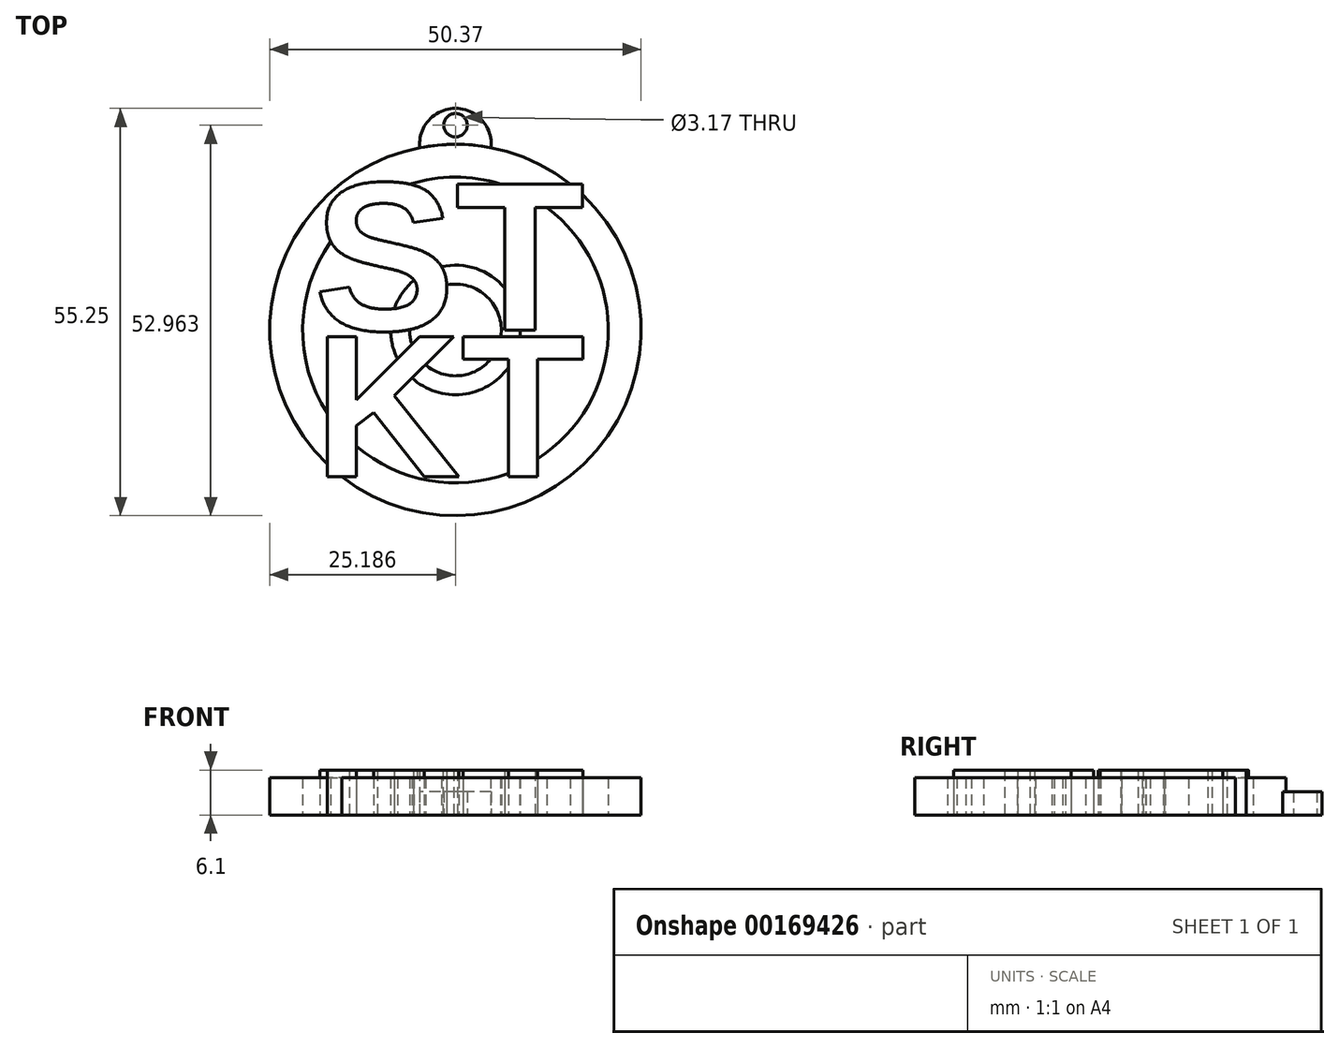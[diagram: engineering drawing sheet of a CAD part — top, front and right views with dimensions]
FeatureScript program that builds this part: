
annotation { "Feature Type Name" : "Feature", "Feature Type Description" : "" }
export const myFeature = defineFeature(function(context is Context, id is Id, definition is map)
    precondition{}
    {
        {
            var Q0;
            Q0=qCreatedBy(makeId("Top.planeOp"),FACE);
            var sketch = newSketch(context, id + "F0", { "sketchPlane" : qUnion([Q0])});
            skText(sketch, "E0", { "text": "ST", "fontName": "Arimo-Bold.ttf"});
            skText(sketch, "E1", { "text": "KT", "fontName": "Arimo-Bold.ttf"});
            skCircle(sketch, "E2", {"center": v(10.39, -1.09) * mm, "radius": 20.73 * mm});
            skCircle(sketch, "E3", {"center": v(10.39, -1.09) * mm, "radius": 25.19 * mm});
            skCircle(sketch, "E4", {"center": v(10.39, 26.68) * mm, "radius": 1.59 * mm});
            skArc(sketch, "E5", {"start": v(15.23, 23.63) * mm, "mid": v(10.39, 28.97) * mm, "end": v(5.54, 23.63) * mm});
            skCircle(sketch, "E6", {"center": v(10.39, -1.09) * mm, "radius": 6.22 * mm});
            skCircle(sketch, "E7", {"center": v(10.39, -1.09) * mm, "radius": 8.79 * mm});
            const initialGuessF0  = {"E0": [-0.00886, -0.00109, 1, 0, 0.02073], "E1": [-0.00886, -0.021, 1, 0, 0.0199]};
            skSetInitialGuess(sketch, initialGuessF0);
            skSolve(sketch);
        }
        {
            var Q0;
            {var subQ0=sQuery(id+"F0.wireOp",EDGE,"E0.sketch_text.stroke-31");Q0=makeQuery(id+"F0.imprint","IMPRINT",FACE,{"disambiguationData":[TD([[makeQuery(id+"F0.imprint","IMPRINT",EDGE,{"derivedFrom":subQ0}),-1.0]])]});}
            var Q1;
            {var subQ1=sQuery(id+"F0.wireOp",EDGE,"E0.sketch_text.stroke-36");var subQ7=sQuery(id+"F0.wireOp",EDGE,"E3");var subQ9=makeQuery(id+"F0.imprint","INTERSECT",VERTEX,{"derivedFrom":[subQ1,subQ7]});Q1=makeQuery(id+"F0.imprint","IMPRINT",FACE,{"disambiguationData":[TD([[makeQuery(id+"F0.imprint","IMPRINT",EDGE,{"disambiguationData":[TD([[subQ9,1.0]])],"derivedFrom":subQ1}),-1.0]])]});}
            var Q2;
            {var subQ0=sQuery(id+"F0.wireOp",EDGE,"E0.sketch_text.stroke-37");var subQ1=sQuery(id+"F0.wireOp",EDGE,"E0.sketch_text.stroke-36");var subQ2=makeQuery(id+"F0.imprint","INTERSECT",VERTEX,{"derivedFrom":[subQ1,subQ0]});Q2=makeQuery(id+"F0.imprint","IMPRINT",FACE,{"disambiguationData":[TD([[makeQuery(id+"F0.imprint","IMPRINT",EDGE,{"disambiguationData":[TD([[subQ2,1.0]])],"derivedFrom":subQ1}),-1.0]])]});}
            var Q3;
            {var subQ6=sQuery(id+"F0.wireOp",EDGE,"E0.sketch_text.stroke-15");Q3=makeQuery(id+"F0.imprint","IMPRINT",FACE,{"disambiguationData":[TD([[makeQuery(id+"F0.imprint","IMPRINT",EDGE,{"derivedFrom":subQ6}),-1.0]])]});}
            var Q4;
            {var subQ0=sQuery(id+"F0.wireOp",EDGE,"E0.sketch_text.stroke-19");Q4=makeQuery(id+"F0.imprint","IMPRINT",FACE,{"disambiguationData":[TD([[makeQuery(id+"F0.imprint","IMPRINT",EDGE,{"derivedFrom":subQ0}),-1.0]])]});}
            var Q5;
            Q5=makeQuery(id+"F0.imprint","IMPRINT",FACE,{"disambiguationData":[TD([[makeQuery(id+"F0.imprint","IMPRINT",EDGE,{"derivedFrom":sQuery(id+"F0.wireOp",EDGE,"E0.sketch_text.stroke-0")}),-1.0]])]});
            var Q6;
            Q6=makeQuery(id+"F0.imprint","IMPRINT",FACE,{"disambiguationData":[TD([[makeQuery(id+"F0.imprint","IMPRINT",EDGE,{"derivedFrom":sQuery(id+"F0.wireOp",EDGE,"E1.sketch_text.stroke-0")}),-1.0]])]});
            var Q7;
            {var subQ0=sQuery(id+"F0.wireOp",EDGE,"E1.sketch_text.stroke-15");Q7=makeQuery(id+"F0.imprint","IMPRINT",FACE,{"disambiguationData":[TD([[makeQuery(id+"F0.imprint","IMPRINT",EDGE,{"derivedFrom":subQ0}),-1.0]])]});}
            var Q8;
            {var subQ1=sQuery(id+"F0.wireOp",EDGE,"E1.sketch_text.stroke-2");var subQ7=sQuery(id+"F0.wireOp",EDGE,"E1.sketch_text.stroke-3");var subQ8=makeQuery(id+"F0.imprint","INTERSECT",VERTEX,{"derivedFrom":[subQ1,subQ7]});Q8=makeQuery(id+"F0.imprint","IMPRINT",FACE,{"disambiguationData":[TD([[makeQuery(id+"F0.imprint","IMPRINT",EDGE,{"disambiguationData":[TD([[subQ8,1.0]])],"derivedFrom":subQ1}),-1.0]])]});}
            var Q9;
            {var subQ0=sQuery(id+"F0.wireOp",EDGE,"E1.sketch_text.stroke-4");var subQ1=sQuery(id+"F0.wireOp",EDGE,"E1.sketch_text.stroke-3");var subQ2=makeQuery(id+"F0.imprint","INTERSECT",VERTEX,{"derivedFrom":[subQ1,subQ0]});Q9=makeQuery(id+"F0.imprint","IMPRINT",FACE,{"disambiguationData":[TD([[makeQuery(id+"F0.imprint","IMPRINT",EDGE,{"disambiguationData":[TD([[subQ2,1.0]])],"derivedFrom":subQ1}),-1.0]])]});}
            var Q10;
            {var subQ0=sQuery(id+"F0.wireOp",EDGE,"E1.sketch_text.stroke-13");Q10=makeQuery(id+"F0.imprint","IMPRINT",FACE,{"disambiguationData":[TD([[makeQuery(id+"F0.imprint","IMPRINT",EDGE,{"derivedFrom":subQ0}),-1.0]])]});}
            var Q11;
            {var subQ4=sQuery(id+"F0.wireOp",EDGE,"E0.sketch_text.stroke-9");Q11=makeQuery(id+"F0.imprint","IMPRINT",FACE,{"disambiguationData":[TD([[makeQuery(id+"F0.imprint","IMPRINT",EDGE,{"derivedFrom":subQ4}),-1.0]])]});}
            var Q12;
            {var subQ0=sQuery(id+"F0.wireOp",EDGE,"E0.sketch_text.stroke-2");Q12=makeQuery(id+"F0.imprint","IMPRINT",FACE,{"disambiguationData":[TD([[makeQuery(id+"F0.imprint","IMPRINT",EDGE,{"derivedFrom":subQ0}),-1.0]])]});}
            var Q13;
            {var subQ5=sQuery(id+"F0.wireOp",EDGE,"E0.sketch_text.stroke-1");var subQ12=sQuery(id+"F0.wireOp",EDGE,"E6");var subQ13=makeQuery(id+"F0.imprint","INTERSECT",VERTEX,{"derivedFrom":[subQ5,subQ12]});Q13=makeQuery(id+"F0.imprint","IMPRINT",FACE,{"disambiguationData":[TD([[makeQuery(id+"F0.imprint","IMPRINT",EDGE,{"disambiguationData":[TD([[subQ13,-1.0]])],"derivedFrom":subQ5}),-1.0]])]});}
            var Q14;
            {var subQ0=sQuery(id+"F0.wireOp",EDGE,"E7");var subQ1=sQuery(id+"F0.wireOp",EDGE,"E1.sketch_text.stroke-7");var subQ2=makeQuery(id+"F0.imprint","INTERSECT",VERTEX,{"derivedFrom":[subQ1,subQ0]});Q14=makeQuery(id+"F0.imprint","IMPRINT",FACE,{"disambiguationData":[TD([[makeQuery(id+"F0.imprint","IMPRINT",EDGE,{"disambiguationData":[TD([[subQ2,-1.0]])],"derivedFrom":subQ1}),-1.0]])]});}
            var Q15;
            {var subQ0=sQuery(id+"F0.wireOp",EDGE,"E1.sketch_text.stroke-8");Q15=makeQuery(id+"F0.imprint","IMPRINT",FACE,{"disambiguationData":[TD([[makeQuery(id+"F0.imprint","IMPRINT",EDGE,{"derivedFrom":subQ0}),-1.0]])]});}
            var Q16;
            {var subQ1=sQuery(id+"F0.wireOp",EDGE,"E1.sketch_text.stroke-15");var subQ7=sQuery(id+"F0.wireOp",EDGE,"E1.sketch_text.stroke-14");var subQ8=makeQuery(id+"F0.imprint","INTERSECT",VERTEX,{"derivedFrom":[subQ7,subQ1]});Q16=makeQuery(id+"F0.imprint","IMPRINT",FACE,{"disambiguationData":[TD([[makeQuery(id+"F0.imprint","IMPRINT",EDGE,{"disambiguationData":[TD([[subQ8,1.0]])],"derivedFrom":subQ7}),-1.0]])]});}
            var Q17;
            {var subQ0=sQuery(id+"F0.wireOp",EDGE,"E1.sketch_text.stroke-18");Q17=makeQuery(id+"F0.imprint","IMPRINT",FACE,{"disambiguationData":[TD([[makeQuery(id+"F0.imprint","IMPRINT",EDGE,{"derivedFrom":subQ0}),-1.0]])]});}
            var Q18;
            {var subQ0=sQuery(id+"F0.wireOp",EDGE,"E0.sketch_text.stroke-33");var subQ1=sQuery(id+"F0.wireOp",EDGE,"E0.sketch_text.stroke-32");var subQ2=makeQuery(id+"F0.imprint","INTERSECT",VERTEX,{"derivedFrom":[subQ1,subQ0]});Q18=makeQuery(id+"F0.imprint","IMPRINT",FACE,{"disambiguationData":[TD([[makeQuery(id+"F0.imprint","IMPRINT",EDGE,{"disambiguationData":[TD([[subQ2,1.0]])],"derivedFrom":subQ1}),-1.0]])]});}
            extrude(context, id + "F1", {"entities" : qUnion([Q0, Q1, Q2, Q3, Q4, Q5, Q6, Q7, Q8, Q9, Q10, Q11, Q12, Q13, Q14, Q15, Q16, Q17, Q18]), "depth" : 6.1 * mm});
        }
        {
            var Q0;
            {var subQ15=sQuery(id+"F0.wireOp",EDGE,"E0.sketch_text.stroke-15");Q0=makeQuery(id+"F0.imprint","IMPRINT",FACE,{"disambiguationData":[TD([[makeQuery(id+"F0.imprint","IMPRINT",EDGE,{"derivedFrom":subQ15}),1.0]])]});}
            var Q1;
            {var subQ14=sQuery(id+"F0.wireOp",EDGE,"E1.sketch_text.stroke-13");Q1=makeQuery(id+"F0.imprint","IMPRINT",FACE,{"disambiguationData":[TD([[makeQuery(id+"F0.imprint","IMPRINT",EDGE,{"derivedFrom":subQ14}),1.0]])]});}
            extrude(context, id + "F2", {"entities" : qUnion([Q0, Q1]), "operationType" : NewBodyOperationType.ADD, "depth" : 5.08 * mm});
        }
        {
            var Q0;
            Q0=makeQuery(id+"F0.imprint","IMPRINT",FACE,{"disambiguationData":[TD([[makeQuery(id+"F0.imprint","IMPRINT",EDGE,{"derivedFrom":sQuery(id+"F0.wireOp",EDGE,"E4")}),-1.0]])]});
            extrude(context, id + "F3", {"entities" : qUnion([Q0]), "operationType" : NewBodyOperationType.ADD, "depth" : 3.17 * mm});
        }
        {
            var Q0;
            {var subQ5=sQuery(id+"F0.wireOp",EDGE,"E0.sketch_text.stroke-30");var subQ6=sQuery(id+"F0.wireOp",EDGE,"E0.sketch_text.stroke-29");var subQ7=makeQuery(id+"F0.imprint","INTERSECT",VERTEX,{"derivedFrom":[subQ6,subQ5]});Q0=makeQuery(id+"F0.imprint","IMPRINT",FACE,{"disambiguationData":[TD([[makeQuery(id+"F0.imprint","IMPRINT",EDGE,{"disambiguationData":[TD([[subQ7,1.0]])],"derivedFrom":subQ6}),1.0]])]});}
            var Q1;
            {var subQ0=sQuery(id+"F0.wireOp",EDGE,"E6");var subQ1=sQuery(id+"F0.wireOp",EDGE,"E1.sketch_text.stroke-9");var subQ2=makeQuery(id+"F0.imprint","INTERSECT",VERTEX,{"derivedFrom":[subQ1,subQ0]});Q1=makeQuery(id+"F0.imprint","IMPRINT",FACE,{"disambiguationData":[TD([[makeQuery(id+"F0.imprint","IMPRINT",EDGE,{"disambiguationData":[TD([[subQ2,-1.0]])],"derivedFrom":subQ1}),1.0]])]});}
            var Q2;
            {var subQ0=sQuery(id+"F0.wireOp",EDGE,"E6");var subQ1=sQuery(id+"F0.wireOp",EDGE,"E0.sketch_text.stroke-1");var subQ2=makeQuery(id+"F0.imprint","INTERSECT",VERTEX,{"derivedFrom":[subQ1,subQ0]});Q2=makeQuery(id+"F0.imprint","IMPRINT",FACE,{"disambiguationData":[TD([[makeQuery(id+"F0.imprint","IMPRINT",EDGE,{"disambiguationData":[TD([[subQ2,-1.0]])],"derivedFrom":subQ1}),1.0]])]});}
            var Q3;
            {var subQ0=sQuery(id+"F0.wireOp",EDGE,"E0.sketch_text.stroke-8");var subQ1=sQuery(id+"F0.wireOp",EDGE,"E0.sketch_text.stroke-7");var subQ2=makeQuery(id+"F0.imprint","INTERSECT",VERTEX,{"derivedFrom":[subQ1,subQ0]});Q3=makeQuery(id+"F0.imprint","IMPRINT",FACE,{"disambiguationData":[TD([[makeQuery(id+"F0.imprint","IMPRINT",EDGE,{"disambiguationData":[TD([[subQ2,1.0]])],"derivedFrom":subQ1}),1.0]])]});}
            extrude(context, id + "F4", {"entities" : qUnion([Q0, Q1, Q2, Q3]), "operationType" : NewBodyOperationType.ADD, "depth" : 5.08 * mm});
        }
    });
